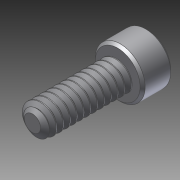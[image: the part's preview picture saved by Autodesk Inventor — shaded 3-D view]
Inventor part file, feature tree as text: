
AUTODESK INVENTOR PART (.ipt)
format: ipt  version: 2014 SP1 (Build 180222100, 222)  size: 592,384 bytes
history: native  units: in
note: dims shown in document units (in); Inventor stores cm internally (conversion verified against a paired STEP export)
features: chamfer x1, other x1, imported_body x1
ambient origin geometry x8: Origin, YZ Plane, XZ Plane, XY Plane, X Axis, Y Axis, Z Axis, Center Point
bodies: Body1 (feature_tree)
feature tree (3):
  chamfer  "Chamfer1"  [1 undecoded]
  other  "91251A107_91251A107.ipt1"
  imported_body  "Base1"
note: 1 required parameter value undecoded (feature->parameter linkage not recoverable at this tier; creation-order binding heuristic only, values carry confidence <= 0.55)
